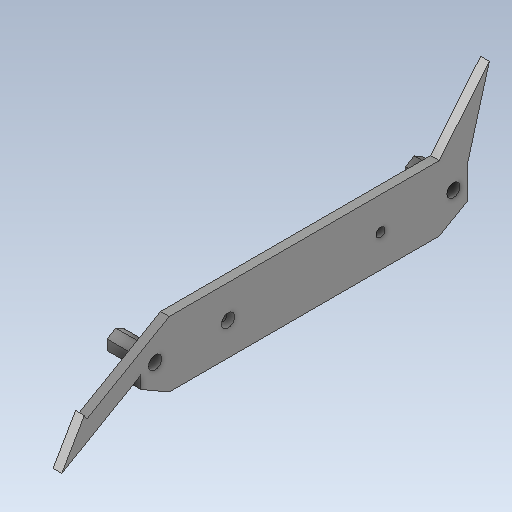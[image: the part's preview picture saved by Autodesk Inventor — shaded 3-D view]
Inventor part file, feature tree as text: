
AUTODESK INVENTOR PART (.ipt)
format: ipt  version: 2020 (Build 240168000, 168)  size: 174,080 bytes
history: native  units: in
note: dims shown in document units (in); Inventor stores cm internally (conversion verified against a paired STEP export)
features: other x3, extrude x2, sketch x2
ambient origin geometry x8: Origin, YZ Plane, XZ Plane, XY Plane, X Axis, Y Axis, Z Axis, Center Point
bodies: Solid1 (feature_tree)
feature tree (7):
  other  "HexWheelGuard.ipt"
  extrude  "Extrusion1"  Depth=0.315in
  extrude  "Extrusion2"  Depth=0.3937in
  other  "Solid1::HexWheelGuard.ipt"
  other  "TaggingFeature2"
  sketch  "Sketch1"  dims[d1=0.3937in d2=0.315in]
  sketch  "Sketch2"  dims[d3=60.0deg d4=1.4843in d5=0.0787in d6=0.3937in d7=0.0in d10=0.3937in d11=1.1024in d12=0.3937in d13=0.0in]
